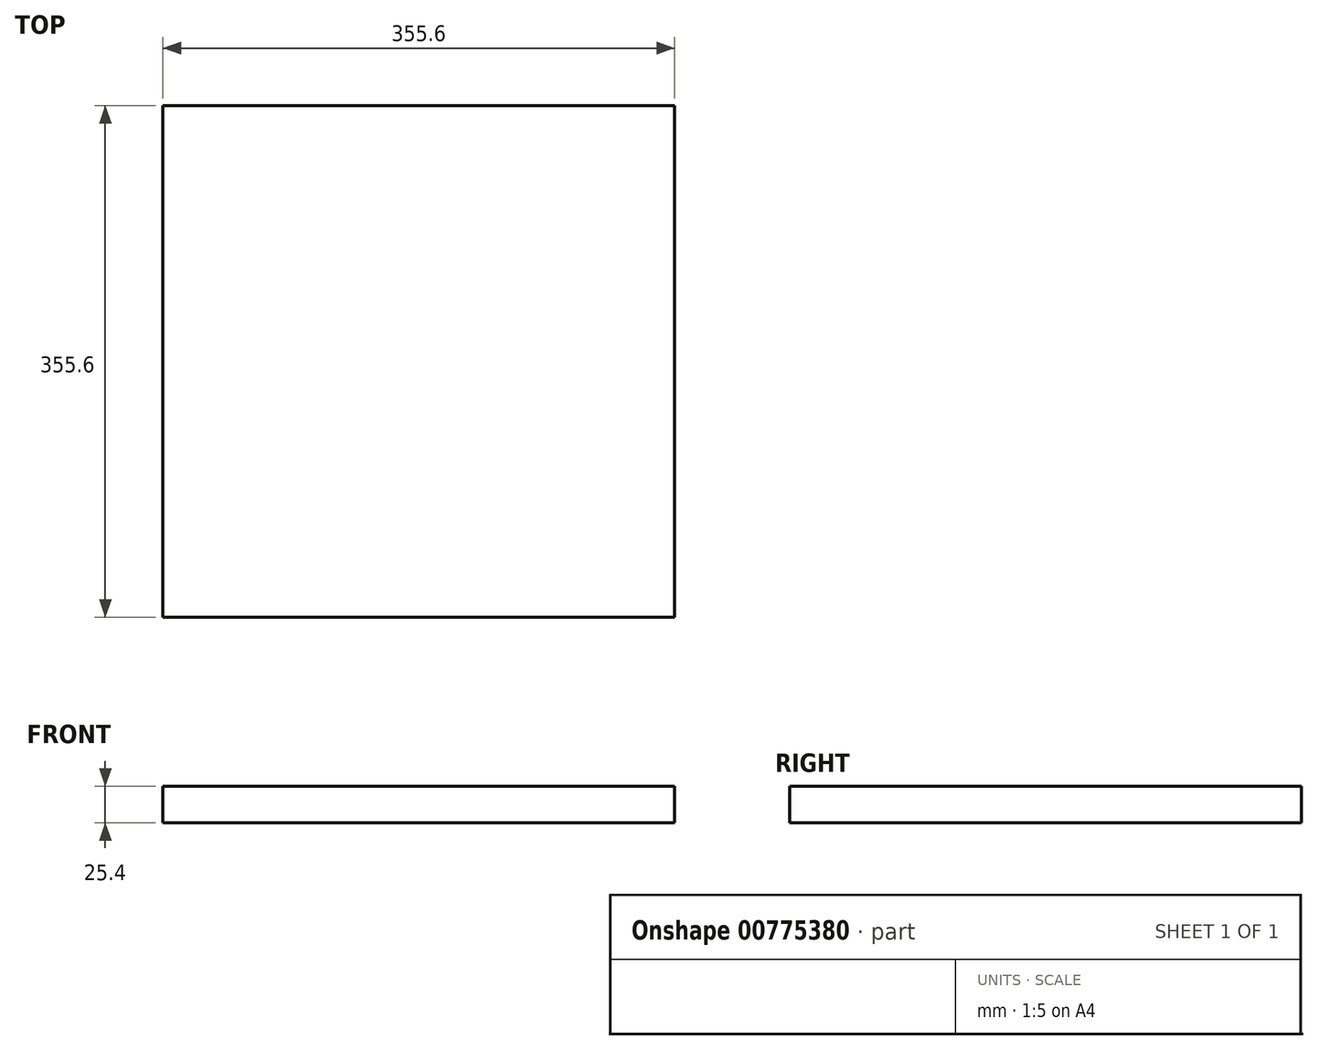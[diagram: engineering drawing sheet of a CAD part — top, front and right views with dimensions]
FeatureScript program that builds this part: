
annotation { "Feature Type Name" : "Feature", "Feature Type Description" : "" }
export const myFeature = defineFeature(function(context is Context, id is Id, definition is map)
    precondition{}
    {
        {
            var Q0;
            Q0=qCreatedBy(makeId("Top.planeOp"),FACE);
            var sketch = newSketch(context, id + "F0", { "sketchPlane" : qUnion([Q0])});
            skLineSegment(sketch, "E0.bottom", {"start": v(-177.8, 177.8) * mm, "end": v(177.8, 177.8) * mm});
            skLineSegment(sketch, "E0.top", {"start": v(-177.8, -177.8) * mm, "end": v(177.8, -177.8) * mm});
            skLineSegment(sketch, "E0.left", {"start": v(-177.8, 177.8) * mm, "end": v(-177.8, -177.8) * mm});
            skLineSegment(sketch, "E0.right", {"start": v(177.8, 177.8) * mm, "end": v(177.8, -177.8) * mm});
            skPoint(sketch, "E0.middle", {"position": v(0, 0) * mm});
            skSolve(sketch);
        }
        {
            var Q0;
            Q0=makeQuery(id+"F0.imprint","IMPRINT",FACE,{"disambiguationData":[TD([[makeQuery(id+"F0.imprint","IMPRINT",EDGE,{"derivedFrom":sQuery(id+"F0.wireOp",EDGE,"E0.bottom")}),-1.0]])]});
            extrude(context, id + "F1", {"entities" : qUnion([Q0]), "endBound" : BoundingType.SYMMETRIC, "depth" : 25.4 * mm, "offsetDistance" : 25.4 * mm});
        }
    });
